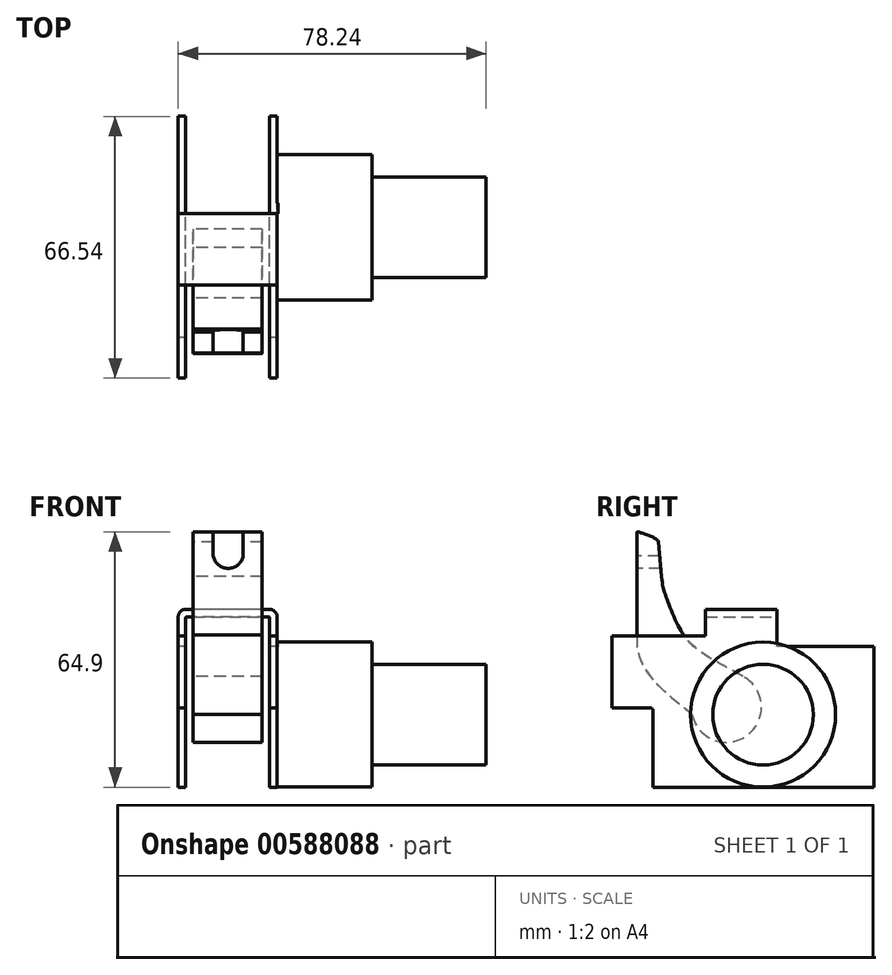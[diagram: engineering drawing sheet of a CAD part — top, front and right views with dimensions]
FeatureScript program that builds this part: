
annotation { "Feature Type Name" : "Feature", "Feature Type Description" : "" }
export const myFeature = defineFeature(function(context is Context, id is Id, definition is map)
    precondition{}
    {
        {
            var Q0;
            Q0=qCreatedBy(makeId("Right.planeOp"),FACE);
            var sketch = newSketch(context, id + "F0", { "sketchPlane" : qUnion([Q0])});
            skCircle(sketch, "E0", {"center": v(0, 0) * mm, "radius": 18.43 * mm});
            skSolve(sketch);
        }
        {
            var Q0;
            Q0 = qSketchRegion(id + "F0", true);
            extrude(context, id + "F1", {"entities" : qUnion([Q0]), "depth" : 24.13 * mm, "offsetDistance" : 25.4 * mm});
        }
        {
            var Q0;
            Q0=makeQuery(id+"F1.opExtrude","CAP_FACE",FACE,{"disambiguationData":[OSD([sQuery(id+"F0.wireOp",EDGE,"E0")])],"isStart":false});
            var sketch = newSketch(context, id + "F2", { "sketchPlane" : qUnion([Q0])});
            skCircle(sketch, "E1", {"center": v(0, 0) * mm, "radius": 12.79 * mm});
            skSolve(sketch);
        }
        {
            var Q0;
            Q0 = qSketchRegion(id + "F2", true);
            extrude(context, id + "F3", {"entities" : qUnion([Q0]), "operationType" : NewBodyOperationType.ADD, "depth" : 28.96 * mm, "offsetDistance" : 25.4 * mm});
        }
        {
            var Q0;
            Q0=qCreatedBy(makeId("Front.planeOp"),FACE);
            var sketch = newSketch(context, id + "F4", { "sketchPlane" : qUnion([Q0])});
            skLineSegment(sketch, "E2", {"start": v(0, -18.44) * mm, "end": v(0, 24.82) * mm});
            skLineSegment(sketch, "E3", {"start": v(-1.9, 26.72) * mm, "end": v(-23.24, 26.72) * mm});
            skLineSegment(sketch, "E4", {"start": v(-25.15, 24.82) * mm, "end": v(-25.15, -18.44) * mm});
            skLineSegment(sketch, "E5.0", {"start": v(-23.24, 24.56) * mm, "end": v(-23.24, -18.44) * mm});
            skLineSegment(sketch, "E5.1", {"start": v(-2.16, 24.82) * mm, "end": v(-22.99, 24.82) * mm});
            skLineSegment(sketch, "E5.2", {"start": v(-1.9, -18.44) * mm, "end": v(-1.9, 24.56) * mm});
            skLineSegment(sketch, "E6", {"start": v(0, -18.44) * mm, "end": v(-1.9, -18.44) * mm});
            skLineSegment(sketch, "E7", {"start": v(-23.24, -18.44) * mm, "end": v(-25.15, -18.44) * mm});
            skPoint(sketch, "E8.visualSharp", {"position": v(0, 26.72) * mm});
            skArc(sketch, "E8.filletArc", {"start": v(0, 24.82) * mm, "mid": v(-0.56, 26.17) * mm, "end": v(-1.9, 26.72) * mm});
            skPoint(sketch, "E9.visualSharp", {"position": v(-25.15, 26.72) * mm});
            skArc(sketch, "E9.filletArc", {"start": v(-23.24, 26.72) * mm, "mid": v(-24.59, 26.17) * mm, "end": v(-25.15, 24.82) * mm});
            skLineSegment(sketch, "E10.filletArc", {"start": v(-1.9, 24.82) * mm, "end": v(-1.9, 24.82) * mm});
            skLineSegment(sketch, "E11.filletArc", {"start": v(-23.24, 24.82) * mm, "end": v(-23.24, 24.82) * mm});
            skArc(sketch, "E12.filletArc", {"start": v(-1.9, 24.56) * mm, "mid": v(-1.98, 24.74) * mm, "end": v(-2.16, 24.82) * mm});
            skArc(sketch, "E13.filletArc", {"start": v(-22.99, 24.82) * mm, "mid": v(-23.17, 24.74) * mm, "end": v(-23.24, 24.56) * mm});
            skSolve(sketch);
        }
        {
            var Q0;
            Q0 = qSketchRegion(id + "F4", true);
            extrude(context, id + "F5", {"entities" : qUnion([Q0]), "operationType" : NewBodyOperationType.ADD, "depth" : 38.35 * mm, "offsetDistance" : 25.4 * mm, "hasSecondDirection" : true, "secondDirectionOppositeDirection" : true, "secondDirectionDepth" : 28.2 * mm});
        }
        {
            var Q0;
            Q0=makeQuery(id+"F5.opExtrude","SWEPT_FACE",FACE,{"disambiguationData":[OSD([sQuery(id+"F4.wireOp",EDGE,"E4")])]});
            var sketch = newSketch(context, id + "F6", { "sketchPlane" : qUnion([Q0])});
            skLineSegment(sketch, "E14", {"start": v(38.35, -18.44) * mm, "end": v(28, -18.44) * mm});
            skLineSegment(sketch, "E15", {"start": v(28, -18.44) * mm, "end": v(28, 1.07) * mm});
            skLineSegment(sketch, "E16", {"start": v(28.63, 1.7) * mm, "end": v(38.35, 1.7) * mm});
            skLineSegment(sketch, "E17", {"start": v(38.35, 1.7) * mm, "end": v(38.35, -18.44) * mm});
            skPoint(sketch, "E18.visualSharp", {"position": v(28, 1.7) * mm});
            skArc(sketch, "E18.filletArc", {"start": v(28.63, 1.7) * mm, "mid": v(28.18, 1.52) * mm, "end": v(28, 1.07) * mm});
            skLineSegment(sketch, "E19", {"start": v(-28.2, 17.38) * mm, "end": v(-3.5, 17.38) * mm});
            skLineSegment(sketch, "E20", {"start": v(-3.5, 17.38) * mm, "end": v(-3.5, 26.72) * mm});
            skLineSegment(sketch, "E21", {"start": v(14.63, 26.72) * mm, "end": v(14.63, 20.02) * mm});
            skLineSegment(sketch, "E22", {"start": v(14.63, 20.02) * mm, "end": v(38.35, 20.02) * mm});
            skLineSegment(sketch, "E23", {"start": v(-28.2, 17.38) * mm, "end": v(-28.2, 26.72) * mm});
            skLineSegment(sketch, "E24", {"start": v(-28.2, 26.72) * mm, "end": v(-3.5, 26.72) * mm});
            skLineSegment(sketch, "E25", {"start": v(14.63, 26.72) * mm, "end": v(38.35, 26.72) * mm});
            skLineSegment(sketch, "E26", {"start": v(38.35, 26.72) * mm, "end": v(38.35, 20.02) * mm});
            skSolve(sketch);
        }
        {
            var Q0;
            Q0 = qSketchRegion(id + "F6", true);
            extrude(context, id + "F7", {"entities" : qUnion([Q0]), "operationType" : NewBodyOperationType.REMOVE, "oppositeDirection" : true, "depth" : 25.4 * mm, "offsetDistance" : 25.4 * mm});
        }
        {
            var Q0;
            Q0=qCreatedBy(makeId("Right.planeOp"),FACE);
            cPlane(context, id + "F8", {"entities" : qUnion([Q0]), "cplaneType" : CPlaneType.OFFSET, "offset" : 12.57 * mm, "oppositeDirection" : true, "width" : 152.4 * mm, "height" : 152.4 * mm});
        }
        {
            var Q0;
            Q0=qCreatedBy(id+"F8.planeOp",FACE);
            var sketch = newSketch(context, id + "F9", { "sketchPlane" : qUnion([Q0])});
            skCircle(sketch, "E27", {"center": v(-9.32, 1.87) * mm, "radius": 8.9 * mm});
            skLineSegment(sketch, "E28", {"start": v(-32, 20.27) * mm, "end": v(-32, 46.43) * mm});
            skLineSegment(sketch, "E29", {"start": v(-26.55, 43.84) * mm, "end": v(-25.8, 35.1) * mm});
            skFitSpline(sketch, "E30", {"points": [v(-5.11, 9.7) * mm, v(-15.83, 15.92) * mm, v(-21.83, 23.1) * mm, v(-24.83, 30.5) * mm, v(-25.8, 35.1) * mm], "startDerivative": vector(-16.35, 11.02) * mm, "endDerivative": vector(-3.78, 38.6) * mm});
            skFitSpline(sketch, "E31", {"points": [v(-26.55, 43.84) * mm, v(-31.96, 46.45) * mm, v(-32, 46.43) * mm], "startDerivative": vector(-1.2, 4.47) * mm, "endDerivative": vector(0.03, -1.19) * mm});
            skFitSpline(sketch, "E32", {"points": [v(-32, 20.27) * mm, v(-32, 17.42) * mm, v(-28.51, 9.48) * mm, v(-18.01, 0) * mm], "startDerivative": vector(0.57, -29.38) * mm, "endDerivative": vector(-0.43, -2.85) * mm});
            skSolve(sketch);
        }
        {
            var Q0;
            Q0 = qSketchRegion(id + "F9", true);
            extrude(context, id + "F10", {"entities" : qUnion([Q0]), "depth" : 8.76 * mm, "offsetDistance" : 25.4 * mm, "hasSecondDirection" : true, "secondDirectionOppositeDirection" : true, "secondDirectionDepth" : 8.76 * mm});
        }
        {
            var Q0;
            Q0=makeQuery(id+"F10.opExtrude","SWEPT_FACE",FACE,{"disambiguationData":[OSD([sQuery(id+"F9.wireOp",EDGE,"E28")])]});
            var sketch = newSketch(context, id + "F11", { "sketchPlane" : qUnion([Q0])});
            skLineSegment(sketch, "E33", {"start": v(-16.26, 47.63) * mm, "end": v(-8.64, 47.63) * mm});
            skLineSegment(sketch, "E34", {"start": v(-16.26, 47.63) * mm, "end": v(-16.26, 40.34) * mm});
            skLineSegment(sketch, "E35", {"start": v(-8.64, 47.63) * mm, "end": v(-8.64, 40.34) * mm});
            skArc(sketch, "E36", {"start": v(-16.26, 40.34) * mm, "mid": v(-12.45, 37.17) * mm, "end": v(-8.64, 40.34) * mm});
            skSolve(sketch);
        }
        {
            var Q0;
            Q0 = qSketchRegion(id + "F11", true);
            extrude(context, id + "F12", {"entities" : qUnion([Q0]), "operationType" : NewBodyOperationType.REMOVE, "oppositeDirection" : true, "depth" : 25.4 * mm, "offsetDistance" : 25.4 * mm});
        }
        {
            var Q0;
            Q0=makeQuery(id+"F1.opExtrude","SWEPT_BODY",BODY,{"disambiguationData":[OSD([sQuery(id+"F0.wireOp",EDGE,"E0")])]});
            transform(context, id + "F13", {"entities" : qUnion([Q0]), "transformType" : TransformType.TRANSLATION_3D, "dx" : 0 * mm, "dy" : 0 * mm, "dz" : 0 * mm, "makeCopy" : true});
        }
    });
